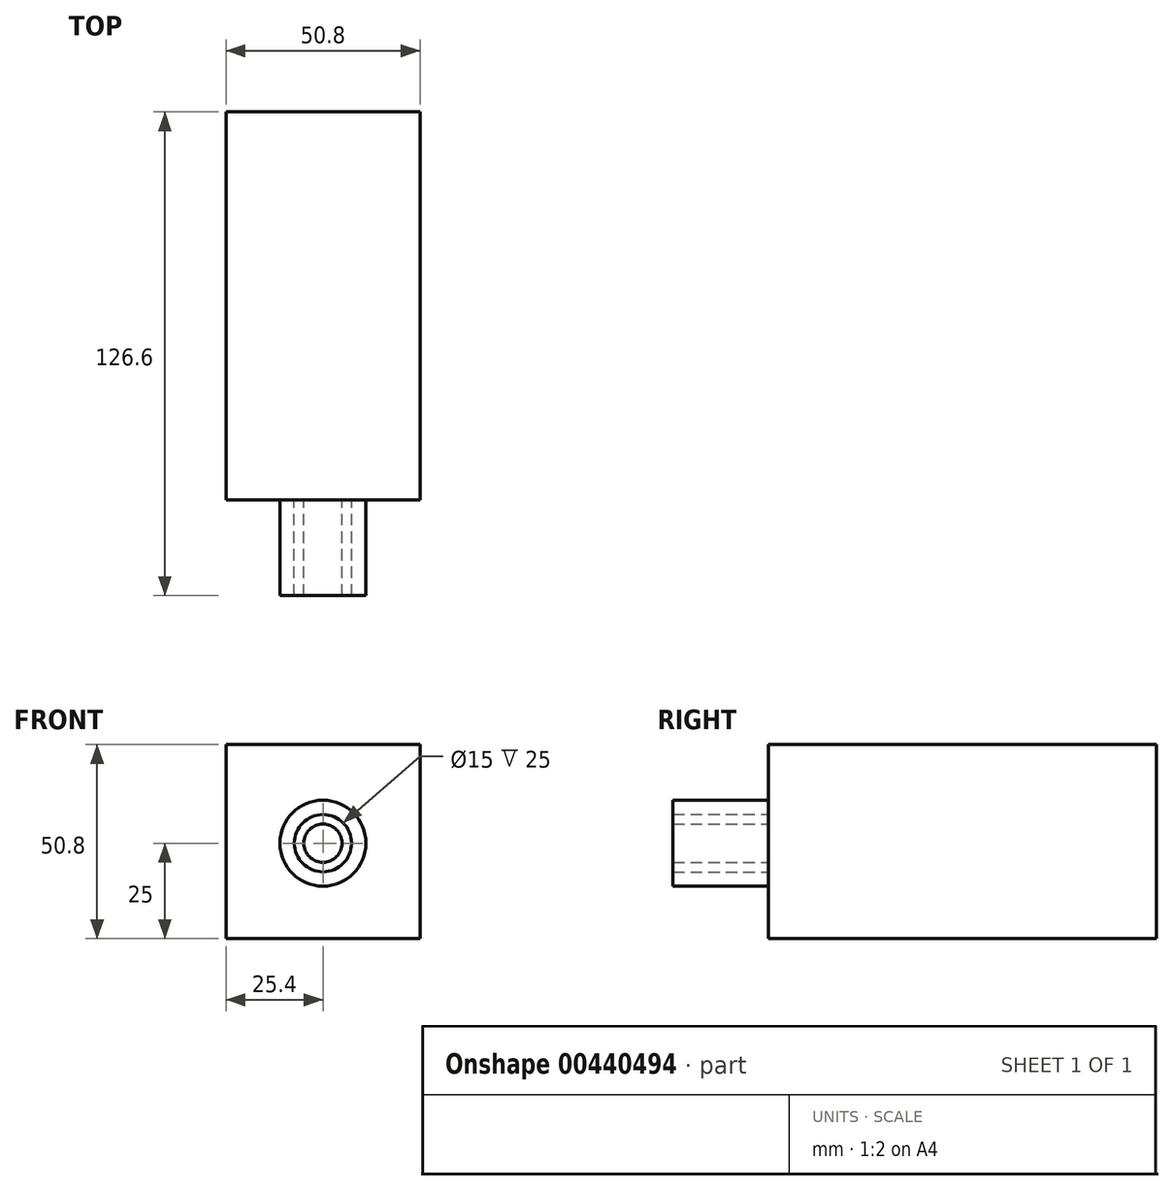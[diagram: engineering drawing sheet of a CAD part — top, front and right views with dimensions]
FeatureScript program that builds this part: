
annotation { "Feature Type Name" : "Feature", "Feature Type Description" : "" }
export const myFeature = defineFeature(function(context is Context, id is Id, definition is map)
    precondition{}
    {
        {
            var Q0;
            Q0=qCreatedBy(makeId("Front.planeOp"),FACE);
            var sketch = newSketch(context, id + "F0", { "sketchPlane" : qUnion([Q0])});
            skLineSegment(sketch, "E0.bottom", {"start": v(25.4, 25.4) * mm, "end": v(-25.4, 25.4) * mm});
            skLineSegment(sketch, "E0.top", {"start": v(25.4, -25.4) * mm, "end": v(-25.4, -25.4) * mm});
            skLineSegment(sketch, "E0.left", {"start": v(25.4, 25.4) * mm, "end": v(25.4, -25.4) * mm});
            skLineSegment(sketch, "E0.right", {"start": v(-25.4, 25.4) * mm, "end": v(-25.4, -25.4) * mm});
            skPoint(sketch, "E0.middle", {"position": v(0, 0) * mm});
            skSolve(sketch);
        }
        {
            var Q0;
            Q0 = qSketchRegion(id + "F0", true);
            extrude(context, id + "F1", {"entities" : qUnion([Q0]), "offsetDistance" : 25 * mm, "depth" : 101.6 * mm});
        }
        {
            var Q0;
            Q0=makeQuery(id+"F1.opExtrude","CAP_FACE",FACE,{"disambiguationData":[OSD([sQuery(id+"F0.wireOp",EDGE,"E0.bottom"),sQuery(id+"F0.wireOp",EDGE,"E0.top"),sQuery(id+"F0.wireOp",EDGE,"E0.left"),sQuery(id+"F0.wireOp",EDGE,"E0.right")])],"isStart":false});
            var sketch = newSketch(context, id + "F2", { "sketchPlane" : qUnion([Q0])});
            skCircle(sketch, "E1", {"center": v(0, -0.4) * mm, "radius": 7.5 * mm});
            skCircle(sketch, "E2", {"center": v(0, -0.4) * mm, "radius": 5 * mm});
            skCircle(sketch, "E3", {"center": v(0, -0.4) * mm, "radius": 11.25 * mm});
            skSolve(sketch);
        }
        {
            var Q0;
            Q0 = qSketchRegion(id + "F2", true);
            var Q1;
            Q1=makeQuery(id+"F2.imprint","IMPRINT",FACE,{"disambiguationData":[TD([[makeQuery(id+"F2.imprint","IMPRINT",EDGE,{"derivedFrom":sQuery(id+"F2.wireOp",EDGE,"E2")}),1.0]])]});
            extrude(context, id + "F3", {"entities" : qUnion([Q0, Q1]), "operationType" : NewBodyOperationType.ADD, "depth" : 25 * mm});
        }
    });
